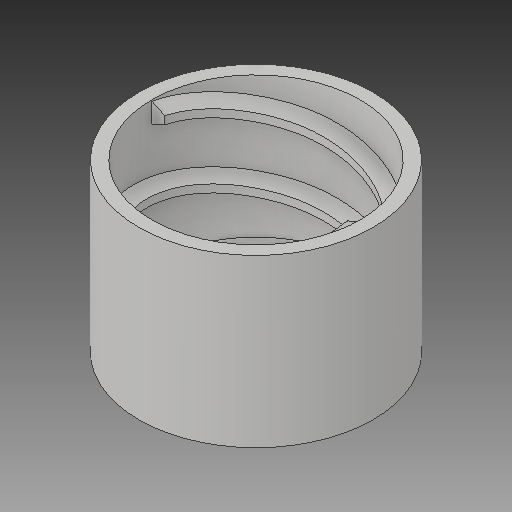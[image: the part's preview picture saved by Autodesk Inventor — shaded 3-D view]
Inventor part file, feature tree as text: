
AUTODESK INVENTOR PART (.ipt)
format: ipt  version: 2019 (Build 230136000, 136)  size: 229,376 bytes
history: imported  units: mm
features: delete_face x3, sketch x2, other x1, imported_body x1
ambient origin geometry x8: Origin, YZ Plane, XZ Plane, XY Plane, X Axis, Y Axis, Z Axis, Center Point
bodies: Volumenkörper1 (imported_parasolid)
feature tree (7):
  other  "Austragung1"
  sketch  "Skizze1"
  sketch  "Skizze2"
  delete_face  "Fläche löschen10"
  delete_face  "Fläche löschen11"
  delete_face  "Fläche löschen12"
  imported_body  NMx_Import_Brep_tag  [imported B-rep: ~5 faces, bbox_mm=None]
